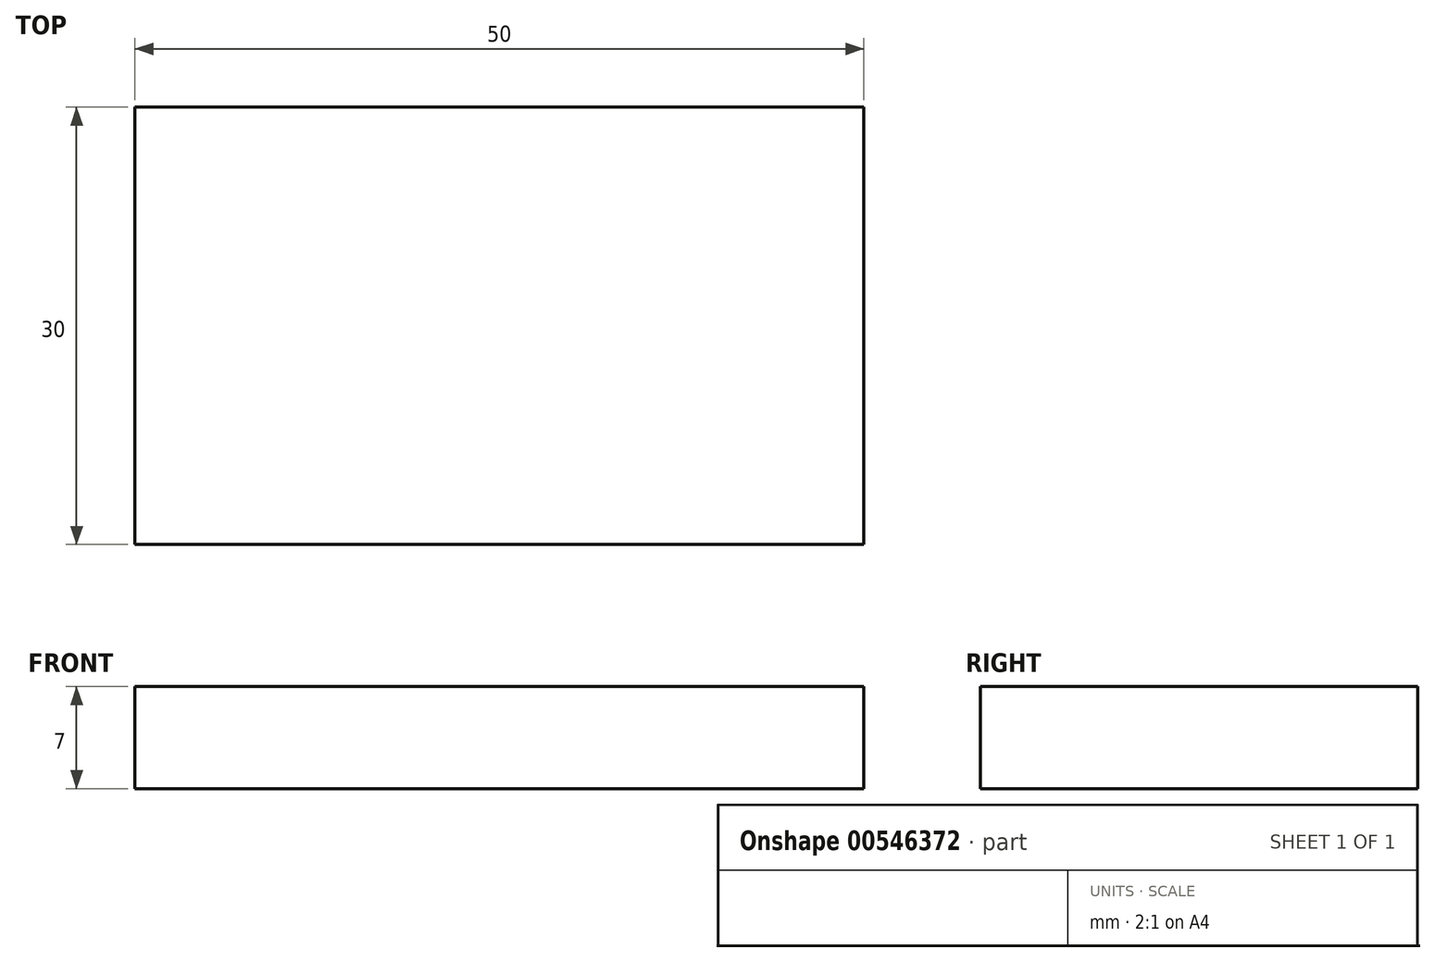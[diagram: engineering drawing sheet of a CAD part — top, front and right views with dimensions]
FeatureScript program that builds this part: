
annotation { "Feature Type Name" : "Feature", "Feature Type Description" : "" }
export const myFeature = defineFeature(function(context is Context, id is Id, definition is map)
    precondition{}
    {
        {
            var Q0;
            Q0=qCreatedBy(makeId("Top.planeOp"),FACE);
            var sketch = newSketch(context, id + "F0", { "sketchPlane" : qUnion([Q0])});
            skLineSegment(sketch, "E0.bottom", {"start": v(0, 0) * mm, "end": v(50, 0) * mm});
            skLineSegment(sketch, "E0.top", {"start": v(0, 30) * mm, "end": v(50, 30) * mm});
            skLineSegment(sketch, "E0.left", {"start": v(0, 0) * mm, "end": v(0, 30) * mm});
            skLineSegment(sketch, "E0.right", {"start": v(50, 0) * mm, "end": v(50, 30) * mm});
            skSolve(sketch);
        }
        {
            var Q0;
            Q0=makeQuery(id+"F0.imprint","IMPRINT",FACE,{"disambiguationData":[TD([[makeQuery(id+"F0.imprint","IMPRINT",EDGE,{"derivedFrom":sQuery(id+"F0.wireOp",EDGE,"E0.bottom")}),1.0]])]});
            extrude(context, id + "F1", {"entities" : qUnion([Q0]), "depth" : 7 * mm, "offsetDistance" : 25 * mm});
        }
    });
